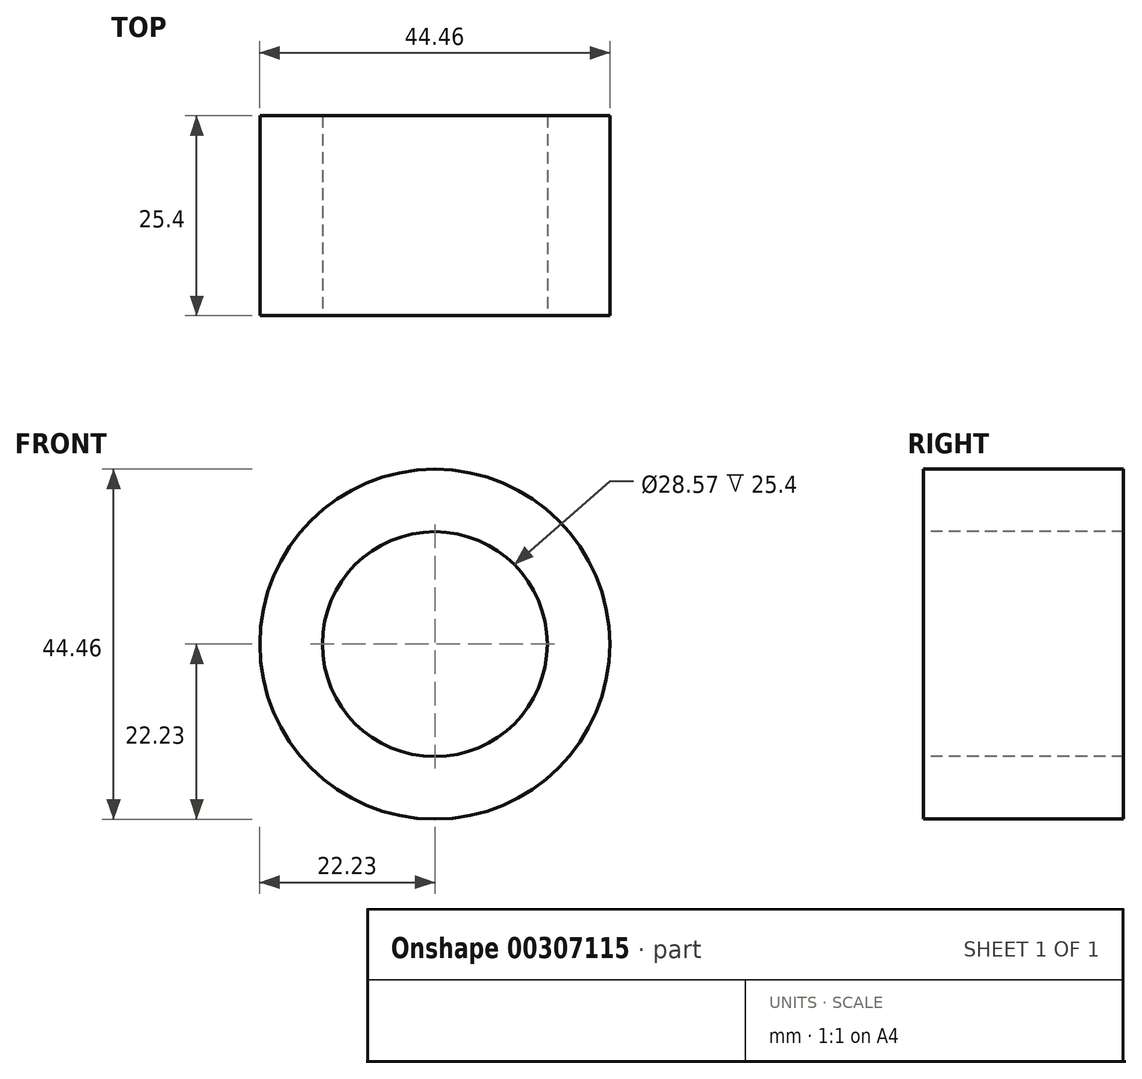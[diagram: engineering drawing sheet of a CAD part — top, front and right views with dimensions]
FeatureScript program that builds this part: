
annotation { "Feature Type Name" : "Feature", "Feature Type Description" : "" }
export const myFeature = defineFeature(function(context is Context, id is Id, definition is map)
    precondition{}
    {
        {
            var Q0;
            Q0=qCreatedBy(makeId("Front.planeOp"),FACE);
            var sketch = newSketch(context, id + "F0", { "sketchPlane" : qUnion([Q0])});
            skCircle(sketch, "E0", {"center": v(0, 0) * mm, "radius": 14.29 * mm});
            skCircle(sketch, "E1", {"center": v(0, 0) * mm, "radius": 22.23 * mm});
            skSolve(sketch);
        }
        {
            var Q0;
            Q0=makeQuery(id+"F0.imprint","IMPRINT",FACE,{"disambiguationData":[TD([[makeQuery(id+"F0.imprint","IMPRINT",EDGE,{"derivedFrom":sQuery(id+"F0.wireOp",EDGE,"E0")}),-1.0]])]});
            var sketch = newSketch(context, id + "F1", { "sketchPlane" : qUnion([Q0])});
            skSolve(sketch);
        }
        {
            var Q0;
            Q0 = qSketchRegion(id + "F1", true);
            var Q1;
            Q1=makeQuery(id+"F0.imprint","IMPRINT",FACE,{"disambiguationData":[TD([[makeQuery(id+"F0.imprint","IMPRINT",EDGE,{"derivedFrom":sQuery(id+"F0.wireOp",EDGE,"E0")}),-1.0]])]});
            extrude(context, id + "F2", {"entities" : qUnion([Q0, Q1]), "oppositeDirection" : true, "depth" : 25.4 * mm});
        }
    });
